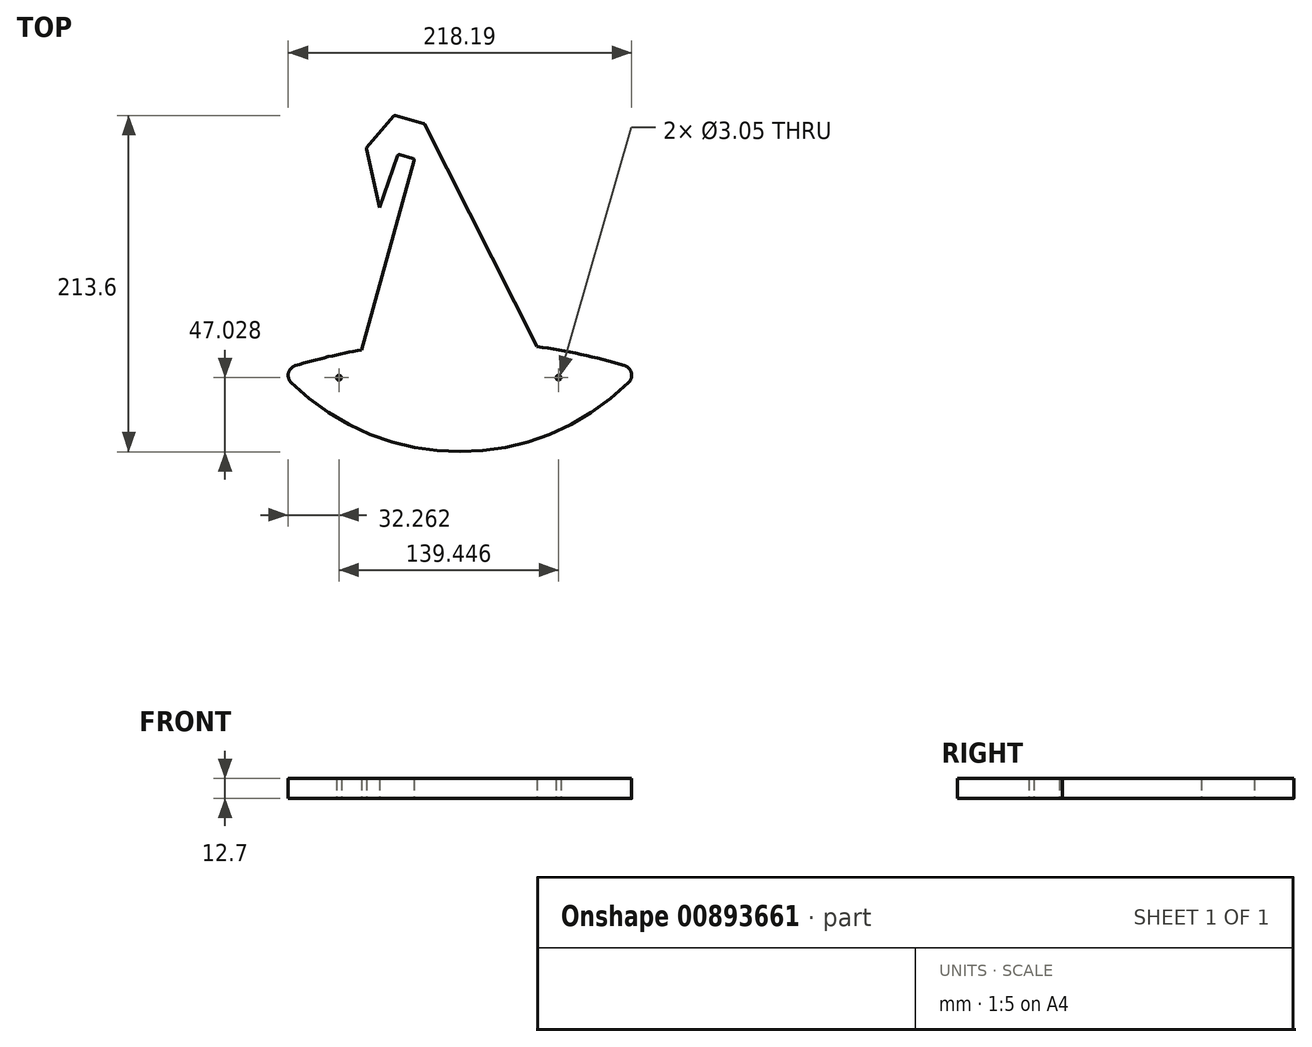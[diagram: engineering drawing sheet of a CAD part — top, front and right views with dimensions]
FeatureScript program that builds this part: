
annotation { "Feature Type Name" : "Feature", "Feature Type Description" : "" }
export const myFeature = defineFeature(function(context is Context, id is Id, definition is map)
    precondition{}
    {
        {
            var Q0;
            Q0=qCreatedBy(makeId("Top.planeOp"),FACE);
            var sketch = newSketch(context, id + "F0", { "sketchPlane" : qUnion([Q0])});
            skArc(sketch, "E0", {"start": v(-75.3, -7.5) * mm, "mid": v(31.92, -51.6) * mm, "end": v(139.13, -7.5) * mm});
            skPoint(sketch, "E1.orphan", {"position": v(-78.83, 0) * mm});
            skArc(sketch, "E2", {"start": v(136.5, 3.08) * mm, "mid": v(108.85, 10.26) * mm, "end": v(80.73, 15.22) * mm});
            skArc(sketch, "E3.trimOffspring", {"start": v(-30.5, 13.1) * mm, "mid": v(-51.73, 8.73) * mm, "end": v(-72.67, 3.08) * mm});
            skPoint(sketch, "E4.visualSharp", {"position": v(-82.38, 0) * mm});
            skArc(sketch, "E4.filletArc", {"start": v(-72.67, 3.08) * mm, "mid": v(-77, -1.46) * mm, "end": v(-75.3, -7.5) * mm});
            skPoint(sketch, "E5.visualSharp", {"position": v(146.22, 0) * mm});
            skArc(sketch, "E5.filletArc", {"start": v(139.13, -7.5) * mm, "mid": v(140.82, -1.46) * mm, "end": v(136.5, 3.08) * mm});
            skPoint(sketch, "E6.start.orphan", {"position": v(2.9, 103.2) * mm});
            skPoint(sketch, "E7.orphan", {"position": v(2.9, 77.52) * mm});
            skPoint(sketch, "E8.trimOffspring.end.orphan", {"position": v(149.77, 0) * mm});
            skLineSegment(sketch, "E9", {"start": v(-34.13, 0) * mm, "end": v(2.86, 133.38) * mm});
            skPoint(sketch, "E10.visualSharp", {"position": v(-36.74, 163.3) * mm});
            skPoint(sketch, "E11.visualSharp", {"position": v(2.7, 170.08) * mm});
            skPoint(sketch, "E12.visualSharp", {"position": v(10.8, 162) * mm});
            skPoint(sketch, "E13.end.orphan", {"position": v(73.72, 0) * mm});
            skLineSegment(sketch, "E14.trimOffspring", {"start": v(9.59, 156.43) * mm, "end": v(88.4, 0) * mm});
            skLineSegment(sketch, "E15", {"start": v(8.9, 157) * mm, "end": v(-9.02, 161.96) * mm});
            skLineSegment(sketch, "E16", {"start": v(-10.14, 161.62) * mm, "end": v(-27.22, 141.49) * mm});
            skLineSegment(sketch, "E17", {"start": v(-27.45, 140.55) * mm, "end": v(-19.03, 103.38) * mm});
            skLineSegment(sketch, "E18", {"start": v(-19.03, 103.38) * mm, "end": v(-7.74, 136.38) * mm});
            skLineSegment(sketch, "E19", {"start": v(-6.43, 137.08) * mm, "end": v(2.1, 134.71) * mm});
            skPoint(sketch, "E20.visualSharp", {"position": v(3.15, 134.42) * mm});
            skArc(sketch, "E20.filletArc", {"start": v(2.86, 133.38) * mm, "mid": v(2.76, 134.2) * mm, "end": v(2.1, 134.71) * mm});
            skPoint(sketch, "E21.visualSharp", {"position": v(-7.41, 137.35) * mm});
            skArc(sketch, "E21.filletArc", {"start": v(-6.43, 137.08) * mm, "mid": v(-7.22, 137) * mm, "end": v(-7.74, 136.38) * mm});
            skPoint(sketch, "E22.visualSharp", {"position": v(-9.7, 162.15) * mm});
            skArc(sketch, "E22.filletArc", {"start": v(-9.02, 161.96) * mm, "mid": v(-9.63, 161.95) * mm, "end": v(-10.14, 161.62) * mm});
            skPoint(sketch, "E23.visualSharp", {"position": v(9.37, 156.86) * mm});
            skArc(sketch, "E23.filletArc", {"start": v(9.59, 156.43) * mm, "mid": v(9.3, 156.78) * mm, "end": v(8.9, 157) * mm});
            skPoint(sketch, "E24.visualSharp", {"position": v(-27.57, 141.08) * mm});
            skArc(sketch, "E24.filletArc", {"start": v(-27.22, 141.49) * mm, "mid": v(-27.45, 141.05) * mm, "end": v(-27.45, 140.55) * mm});
            skCircle(sketch, "E25", {"center": v(77.53, -62.44) * mm, "radius": 1.77 * mm});
            skCircle(sketch, "E26", {"center": v(-44.92, -4.57) * mm, "radius": 1.52 * mm});
            skCircle(sketch, "E27", {"center": v(94.53, -4.57) * mm, "radius": 1.52 * mm});
            skSolve(sketch);
        }
        {
            var Q0;
            Q0=makeQuery(id+"F0.imprint","IMPRINT",FACE,{"disambiguationData":[TD([[makeQuery(id+"F0.imprint","IMPRINT",EDGE,{"derivedFrom":sQuery(id+"F0.wireOp",EDGE,"E0")}),1.0]])]});
            extrude(context, id + "F1", {"entities" : qUnion([Q0]), "depth" : 12.7 * mm, "offsetDistance" : 25.4 * mm});
        }
    });
